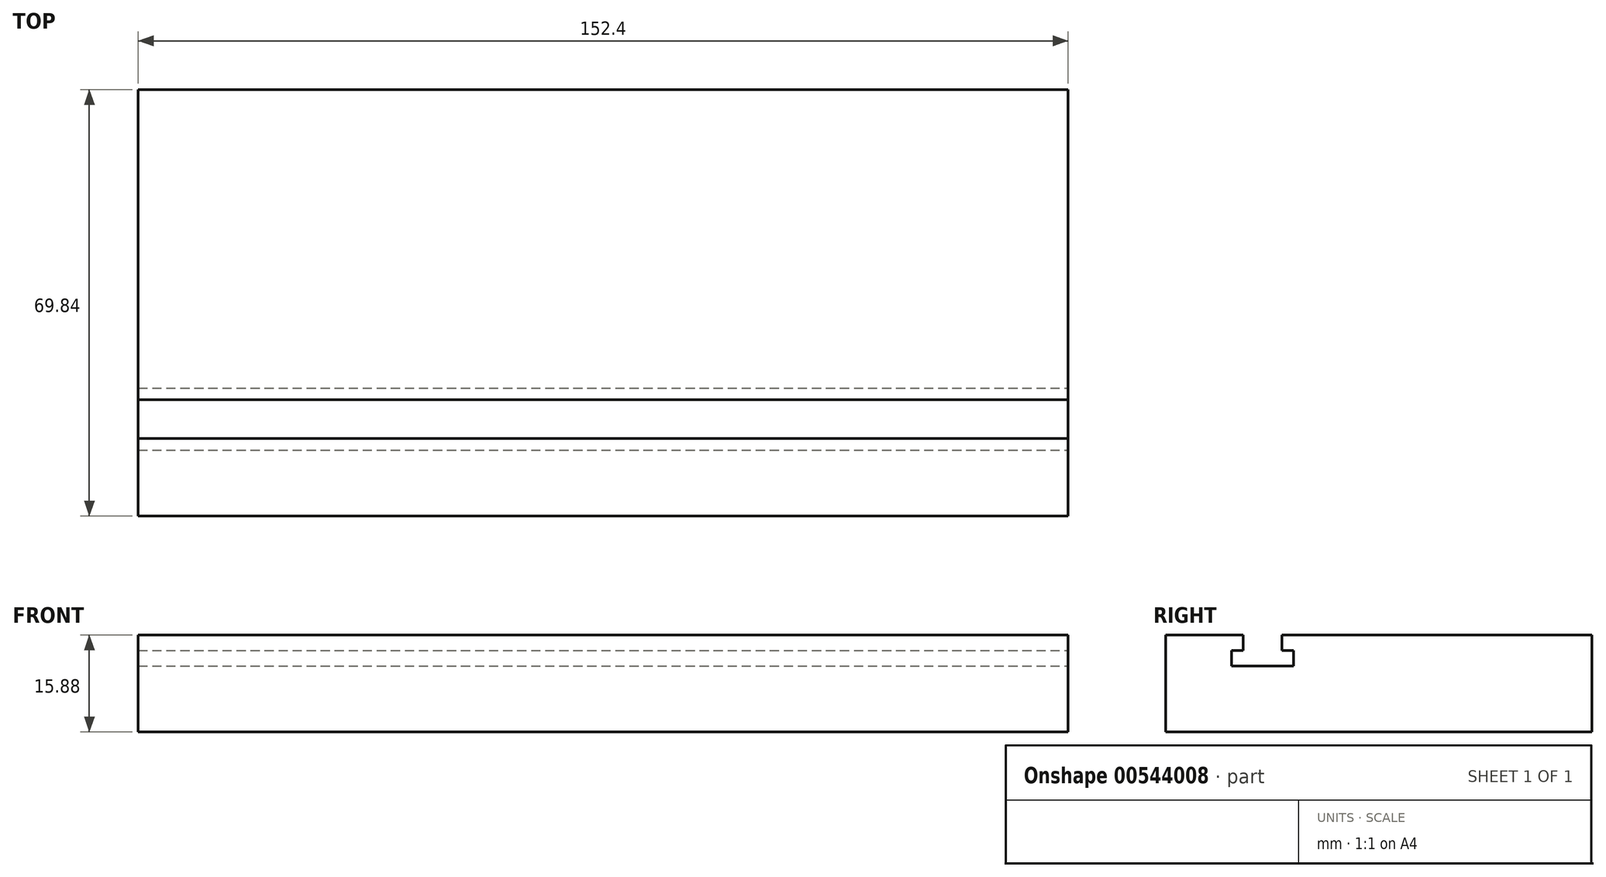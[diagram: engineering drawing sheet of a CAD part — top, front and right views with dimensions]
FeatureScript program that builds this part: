
annotation { "Feature Type Name" : "Feature", "Feature Type Description" : "" }
export const myFeature = defineFeature(function(context is Context, id is Id, definition is map)
    precondition{}
    {
        {
            var Q0;
            Q0=qCreatedBy(makeId("Right.planeOp"),FACE);
            var sketch = newSketch(context, id + "F0", { "sketchPlane" : qUnion([Q0])});
            skLineSegment(sketch, "E0", {"start": v(-34.92, -23.81) * mm, "end": v(34.92, -23.81) * mm});
            skLineSegment(sketch, "E1", {"start": v(34.93, -23.81) * mm, "end": v(34.93, -39.69) * mm});
            skLineSegment(sketch, "E2", {"start": v(34.93, -39.69) * mm, "end": v(-34.93, -39.69) * mm});
            skLineSegment(sketch, "E3", {"start": v(-34.93, -39.69) * mm, "end": v(-34.93, -23.81) * mm});
            skLineSegment(sketch, "E4", {"start": v(0, -23.81) * mm, "end": v(0, 0) * mm, "construction": true});
            skSolve(sketch);
        }
        {
            var Q0;
            Q0 = qSketchRegion(id + "F0", true);
            extrude(context, id + "F1", {"entities" : qUnion([Q0]), "depth" : 76.2 * mm, "offsetDistance" : 25.4 * mm, "hasSecondDirection" : true, "secondDirectionOppositeDirection" : true, "secondDirectionDepth" : 76.2 * mm});
        }
        {
            var Q0;
            Q0=qCreatedBy(makeId("Right.planeOp"),FACE);
            var sketch = newSketch(context, id + "F2", { "sketchPlane" : qUnion([Q0])});
            skLineSegment(sketch, "E5", {"start": v(-15.88, -23.81) * mm, "end": v(-22.23, -23.81) * mm});
            skLineSegment(sketch, "E6", {"start": v(-22.23, -23.81) * mm, "end": v(-22.23, -26.35) * mm});
            skLineSegment(sketch, "E7", {"start": v(-22.23, -26.35) * mm, "end": v(-24.13, -26.35) * mm});
            skLineSegment(sketch, "E8", {"start": v(-24.13, -26.35) * mm, "end": v(-24.13, -28.9) * mm});
            skLineSegment(sketch, "E9", {"start": v(-24.13, -28.9) * mm, "end": v(-13.97, -28.9) * mm});
            skLineSegment(sketch, "E10", {"start": v(-13.97, -28.9) * mm, "end": v(-13.97, -26.35) * mm});
            skLineSegment(sketch, "E11", {"start": v(-13.97, -26.35) * mm, "end": v(-15.88, -26.35) * mm});
            skLineSegment(sketch, "E12", {"start": v(-15.88, -26.35) * mm, "end": v(-15.88, -23.81) * mm});
            skLineSegment(sketch, "E13", {"start": v(-19.05, -28.9) * mm, "end": v(-19.05, -23.81) * mm, "construction": true});
            skSolve(sketch);
        }
        {
            var Q0;
            Q0 = qSketchRegion(id + "F2", true);
            extrude(context, id + "F3", {"entities" : qUnion([Q0]), "operationType" : NewBodyOperationType.REMOVE, "endBound" : BoundingType.THROUGH_ALL, "oppositeDirection" : true, "depth" : 25.4 * mm, "offsetDistance" : 25.4 * mm, "hasSecondDirection" : true, "secondDirectionBound" : BoundingType.THROUGH_ALL, "secondDirectionOppositeDirection" : false, "secondDirectionDepth" : 25.4 * mm});
        }
    });
